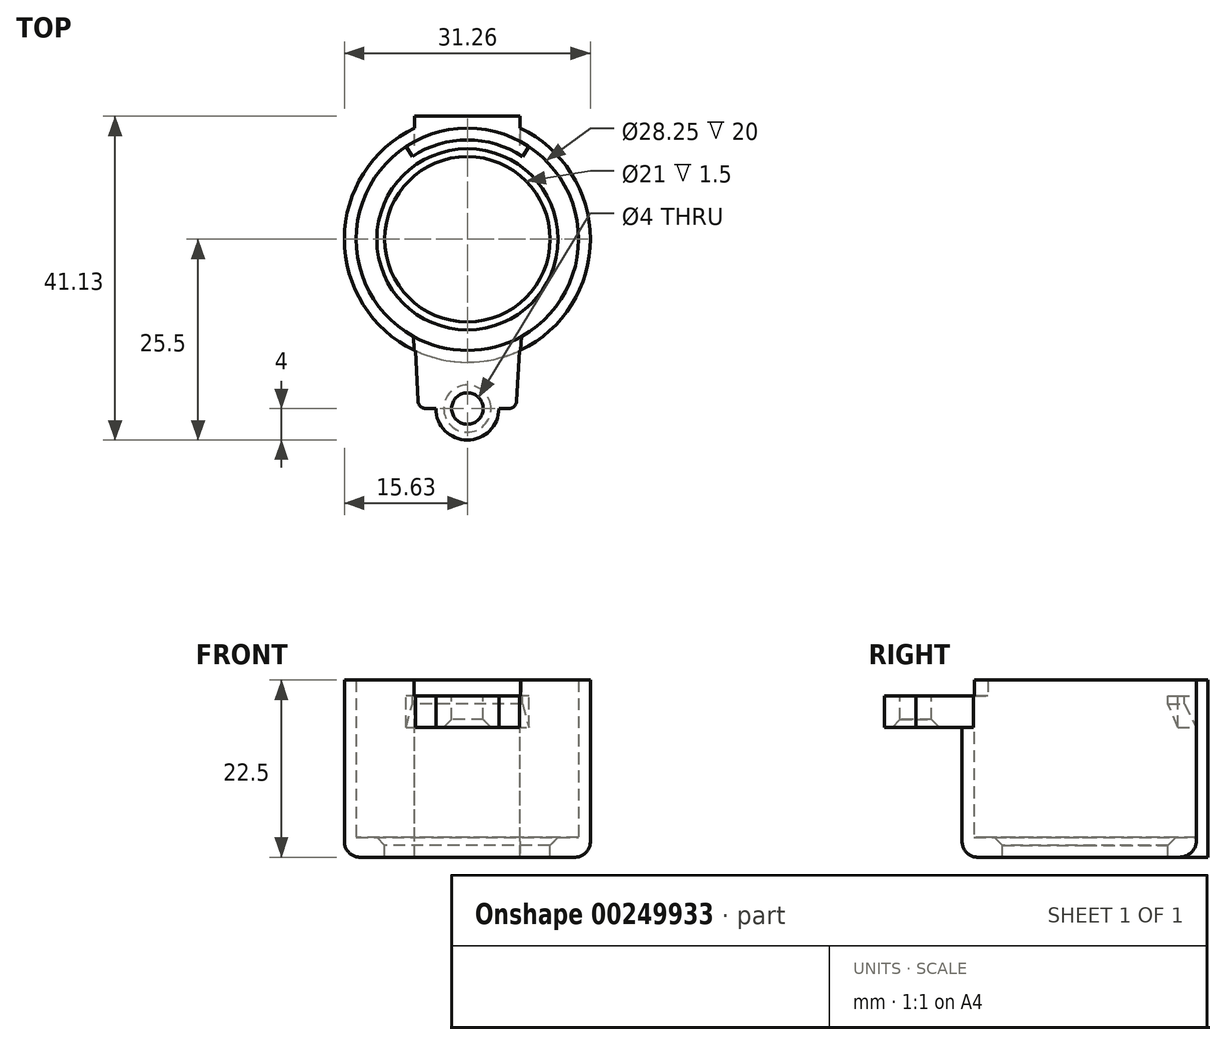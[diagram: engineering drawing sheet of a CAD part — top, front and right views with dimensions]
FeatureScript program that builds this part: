
annotation { "Feature Type Name" : "Feature", "Feature Type Description" : "" }
export const myFeature = defineFeature(function(context is Context, id is Id, definition is map)
    precondition{}
    {
        {
            var Q0;
            Q0=qCreatedBy(makeId("Top.planeOp"),FACE);
            var sketch = newSketch(context, id + "F0", { "sketchPlane" : qUnion([Q0])});
            skCircle(sketch, "E0", {"center": v(0, 0) * mm, "radius": 14.12 * mm});
            skCircle(sketch, "E1", {"center": v(0, 0) * mm, "radius": 15.62 * mm});
            skSolve(sketch);
        }
        {
            var Q0;
            Q0=qSketchRegion(id+"F0",true);
            extrude(context, id + "F1", {"entities" : qUnion([Q0]), "depth" : 20 * mm});
        }
        {
            var Q0;
            Q0=qCreatedBy(makeId("Top.planeOp"),FACE);
            var sketch = newSketch(context, id + "F2", { "sketchPlane" : qUnion([Q0])});
            skCircle(sketch, "E2", {"center": v(0, 0) * mm, "radius": 15.62 * mm});
            skCircle(sketch, "E3", {"center": v(0, 0) * mm, "radius": 10.5 * mm});
            skSolve(sketch);
        }
        {
            var Q0;
            Q0=qSketchRegion(id+"F2",true);
            extrude(context, id + "F3", {"entities" : qUnion([Q0]), "operationType" : NewBodyOperationType.ADD, "oppositeDirection" : true, "depth" : 2.5 * mm});
        }
        {
            var Q0;
            Q0=makeQuery(id+"F1.opExtrude","CAP_FACE",FACE,{"disambiguationData":[OSD([sQuery(id+"F0.wireOp",EDGE,"E0"),sQuery(id+"F0.wireOp",EDGE,"E1")])],"isStart":false});
            var sketch = newSketch(context, id + "F4", { "sketchPlane" : qUnion([Q0])});
            skLineSegment(sketch, "E4", {"start": v(0, -25.51) * mm, "end": v(-6, -25.51) * mm, "construction": true});
            skLineSegment(sketch, "E5", {"start": v(0, -25.51) * mm, "end": v(6, -25.51) * mm});
            skLineSegment(sketch, "E6", {"start": v(-7.2, 0.78) * mm, "end": v(-6, -25.51) * mm, "construction": true});
            skLineSegment(sketch, "E7", {"start": v(7.2, 0.78) * mm, "end": v(6, -25.51) * mm, "construction": true});
            skLineSegment(sketch, "E8", {"start": v(-7.2, 0.78) * mm, "end": v(7.2, 0.78) * mm, "construction": true});
            skPoint(sketch, "E9.end.orphan", {"position": v(-8.39, 27.06) * mm});
            skPoint(sketch, "E10.orphan", {"position": v(8.39, 27.06) * mm});
            skLineSegment(sketch, "E11", {"start": v(0, -25.51) * mm, "end": v(0, 0) * mm, "construction": true});
            skLineSegment(sketch, "E12.0", {"start": v(0, -25.76) * mm, "end": v(6.24, -25.76) * mm});
            skLineSegment(sketch, "E12.1", {"start": v(7.46, 1.03) * mm, "end": v(6.24, -25.76) * mm});
            skLineSegment(sketch, "E12.2", {"start": v(0, -25.76) * mm, "end": v(-6.24, -25.76) * mm});
            skLineSegment(sketch, "E12.3", {"start": v(-7.46, 1.03) * mm, "end": v(-6.24, -25.76) * mm});
            skLineSegment(sketch, "E12.4", {"start": v(-7.46, 1.03) * mm, "end": v(7.46, 1.03) * mm});
            skSolve(sketch);
        }
        {
            var Q0;
            Q0=qSketchRegion(id+"F4",true);
            extrude(context, id + "F5", {"entities" : qUnion([Q0]), "operationType" : NewBodyOperationType.REMOVE, "oppositeDirection" : true, "depth" : 2 * mm});
        }
        {
            var Q0;
            Q0=makeQuery(id+"F1.opExtrude","CAP_FACE",FACE,{"disambiguationData":[OSD([sQuery(id+"F0.wireOp",EDGE,"E0"),sQuery(id+"F0.wireOp",EDGE,"E1")])],"isStart":false});
            var sketch = newSketch(context, id + "F6", { "sketchPlane" : qUnion([Q0])});
            skLineSegment(sketch, "E13.bottom", {"start": v(-6.68, 15.62) * mm, "end": v(0, 15.62) * mm});
            skLineSegment(sketch, "E13.top", {"start": v(-6.68, 14.12) * mm, "end": v(0, 14.12) * mm});
            skCircle(sketch, "E14", {"center": v(0, 0) * mm, "radius": 15.62 * mm, "construction": true});
            skCircle(sketch, "E15", {"center": v(0, 0) * mm, "radius": 14.12 * mm, "construction": true});
            skLineSegment(sketch, "E16", {"start": v(-6.68, 14.12) * mm, "end": v(-6.68, 15.62) * mm});
            skLineSegment(sketch, "E17.MirrorCS", {"start": v(6.68, 15.62) * mm, "end": v(0, 15.62) * mm});
            skLineSegment(sketch, "E18.MirrorCS", {"start": v(6.68, 14.12) * mm, "end": v(6.68, 15.62) * mm});
            skLineSegment(sketch, "E19.MirrorCS", {"start": v(6.68, 14.12) * mm, "end": v(0, 14.12) * mm});
            skSolve(sketch);
        }
        {
            var Q0;
            Q0 = qSketchRegion(id + "F6", true);
            extrude(context, id + "F7", {"entities" : qUnion([Q0]), "operationType" : NewBodyOperationType.ADD, "oppositeDirection" : true, "depth" : 22.5 * mm});
        }
        {
            var Q0;
            Q0=makeQuery(id+"F3.opExtrude","CAP_EDGE",EDGE,{"disambiguationData":[OSD([sQuery(id+"F2.wireOp",EDGE,"E2")])],"isStart":false});
            fillet(context, id + "F8", {"entities" : qUnion([Q0]), "radius" : 2 * mm, "tangentPropagation" : true, "allowEdgeOverflow" : false});
        }
        {
            var Q0;
            Q0=makeQuery(id+"F3.opExtrude","CAP_EDGE",EDGE,{"disambiguationData":[OSD([sQuery(id+"F2.wireOp",EDGE,"E3")])],"isStart":true});
            chamfer(context, id + "F9", {"entities" : qUnion([Q0]), "width" : 1 * mm, "tangentPropagation" : true});
        }
        {
            var Q0;
            Q0=makeQuery(id+"F5.boolean.opBoolean","COPY",FACE,{"derivedFrom":makeQuery(id+"F5.opExtrude","CAP_FACE",FACE,{"disambiguationData":[OSD([sQuery(id+"F4.wireOp",EDGE,"E12.0"),sQuery(id+"F4.wireOp",EDGE,"E12.1"),sQuery(id+"F4.wireOp",EDGE,"E12.2"),sQuery(id+"F4.wireOp",EDGE,"E12.3"),sQuery(id+"F4.wireOp",EDGE,"E12.4")])],"isStart":false})});
            var sketch = newSketch(context, id + "F10", { "sketchPlane" : qUnion([Q0])});
            skArc(sketch, "E20", {"start": v(7.82, 11.76) * mm, "mid": v(0, 14.13) * mm, "end": v(-7.82, 11.76) * mm});
            skArc(sketch, "E21", {"start": v(6.99, 10.52) * mm, "mid": v(0, 12.62) * mm, "end": v(-6.99, 10.52) * mm});
            skLineSegment(sketch, "E22", {"start": v(-6.99, 10.52) * mm, "end": v(-7.82, 11.76) * mm});
            skLineSegment(sketch, "E23", {"start": v(7.82, 11.76) * mm, "end": v(6.99, 10.52) * mm});
            skSolve(sketch);
        }
        {
            var Q0;
            Q0=qSketchRegion(id+"F10",true);
            extrude(context, id + "F11", {"entities" : qUnion([Q0]), "operationType" : NewBodyOperationType.ADD, "oppositeDirection" : true, "depth" : 5 * mm});
        }
        {
            var Q0;
            Q0=makeQuery(id+"F11.opExtrude","CAP_EDGE",EDGE,{"disambiguationData":[OSD([sQuery(id+"F10.wireOp",EDGE,"E21")])],"isStart":false});
            chamfer(context, id + "F12", {"entities" : qUnion([Q0]), "chamferType" : ChamferType.TWO_OFFSETS, "width1" : 2 * mm, "oppositeDirection" : false, "width2" : 4 * mm, "tangentPropagation" : true});
        }
        {
            var Q0;
            Q0=makeQuery(id+"F5.boolean.opBoolean","COPY",FACE,{"derivedFrom":makeQuery(id+"F5.opExtrude","CAP_FACE",FACE,{"disambiguationData":[OSD([sQuery(id+"F4.wireOp",EDGE,"E12.0"),sQuery(id+"F4.wireOp",EDGE,"E12.1"),sQuery(id+"F4.wireOp",EDGE,"E12.2"),sQuery(id+"F4.wireOp",EDGE,"E12.3"),sQuery(id+"F4.wireOp",EDGE,"E12.4")])],"isStart":false})});
            var sketch = newSketch(context, id + "F13", { "sketchPlane" : qUnion([Q0])});
            skPoint(sketch, "E24.endSnap0", {"position": v(0, -14.13) * mm});
            skCircle(sketch, "E25", {"center": v(0, -21.5) * mm, "radius": 2 * mm});
            skCircle(sketch, "E26", {"center": v(0, -21.5) * mm, "radius": 4 * mm, "construction": true});
            skLineSegment(sketch, "E27", {"start": v(0, -25.5) * mm, "end": v(6, -25.5) * mm, "construction": true});
            skLineSegment(sketch, "E28", {"start": v(0, 11.5) * mm, "end": v(8, 11.5) * mm, "construction": true});
            skLineSegment(sketch, "E29", {"start": v(8, 11.5) * mm, "end": v(6, -25.5) * mm, "construction": true});
            skLineSegment(sketch, "E30", {"start": v(0, -25.5) * mm, "end": v(-6, -25.5) * mm, "construction": true});
            skLineSegment(sketch, "E31", {"start": v(0, 11.5) * mm, "end": v(-8, 11.5) * mm, "construction": true});
            skLineSegment(sketch, "E32", {"start": v(-8, 11.5) * mm, "end": v(-6, -25.5) * mm, "construction": true});
            skLineSegment(sketch, "E33", {"start": v(4, -25.5) * mm, "end": v(4, -21.5) * mm, "construction": true});
            skLineSegment(sketch, "E34", {"start": v(-4, -25.5) * mm, "end": v(-4, -21.5) * mm, "construction": true});
            skArc(sketch, "E35", {"start": v(-6.61, -14.16) * mm, "mid": v(0, -15.62) * mm, "end": v(6.61, -14.16) * mm});
            skLineSegment(sketch, "E36", {"start": v(-4, -21.5) * mm, "end": v(-6.22, -21.5) * mm});
            skLineSegment(sketch, "E37", {"start": v(-6.22, -21.5) * mm, "end": v(-6.61, -14.16) * mm});
            skLineSegment(sketch, "E38", {"start": v(4, -21.5) * mm, "end": v(6.22, -21.5) * mm});
            skLineSegment(sketch, "E39", {"start": v(6.22, -21.5) * mm, "end": v(6.61, -14.16) * mm});
            skArc(sketch, "E40", {"start": v(-4, -21.5) * mm, "mid": v(0, -25.5) * mm, "end": v(4, -21.5) * mm});
            skSolve(sketch);
        }
        {
            var Q0;
            Q0 = qSketchRegion(id + "F13", true);
            extrude(context, id + "F14", {"entities" : qUnion([Q0]), "operationType" : NewBodyOperationType.ADD, "oppositeDirection" : true, "depth" : 4 * mm});
        }
        {
            var Q0;
            Q0=makeQuery(id+"F14.opExtrude","SWEPT_EDGE",EDGE,{"disambiguationData":[OSD([sQuery(id+"F13.wireOp",EDGE,"E36"),sQuery(id+"F13.wireOp",EDGE,"E37")])]});
            var Q1;
            Q1=makeQuery(id+"F14.opExtrude","SWEPT_EDGE",EDGE,{"disambiguationData":[OSD([sQuery(id+"F13.wireOp",EDGE,"E38"),sQuery(id+"F13.wireOp",EDGE,"E39")])]});
            var Q2;
            Q2=makeQuery(id+"F7.opExtrude","SWEPT_EDGE",EDGE,{"disambiguationData":[OSD([sQuery(id+"F0.wireOp",EDGE,"E1"),sQuery(id+"F6.wireOp",EDGE,"E18.MirrorCS"),sQuery(id+"F6.wireOp",EDGE,"E19.MirrorCS")])]});
            var Q3;
            Q3=makeQuery(id+"F7.opExtrude","SWEPT_EDGE",EDGE,{"disambiguationData":[OSD([sQuery(id+"F0.wireOp",EDGE,"E1"),sQuery(id+"F6.wireOp",EDGE,"E13.top"),sQuery(id+"F6.wireOp",EDGE,"E16")])]});
            fillet(context, id + "F15", {"entities" : qUnion([Q0, Q1, Q2, Q3]), "radius" : 1 * mm, "tangentPropagation" : true, "allowEdgeOverflow" : false});
        }
        {
            var Q0;
            Q0=makeQuery(id+"F14.opExtrude","CAP_EDGE",EDGE,{"disambiguationData":[OSD([sQuery(id+"F13.wireOp",EDGE,"E25")])],"isStart":false});
            chamfer(context, id + "F16", {"entities" : qUnion([Q0]), "width" : 1 * mm, "tangentPropagation" : true});
        }
    });
